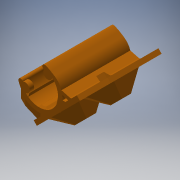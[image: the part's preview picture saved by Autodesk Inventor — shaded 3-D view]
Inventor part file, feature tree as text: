
AUTODESK INVENTOR PART (.ipt)
format: ipt  version: 2017 (Build 210142000, 142)  size: 1,034,752 bytes
history: native  units: in
note: dims shown in document units (in); Inventor stores cm internally (conversion verified against a paired STEP export)
features: other x2, extrude x2, sketch x2
ambient origin geometry x8: Origin, YZ Plane, XZ Plane, XY Plane, X Axis, Y Axis, Z Axis, Center Point
bodies: Solid1 (feature_tree)
feature tree (6):
  other  "10_Support plateau.STEP"
  extrude  "Extrusion1"  Depth=0.3937in TaperAngle=0.0deg
  extrude  "Extrusion2"  [1 undecoded]
  sketch  "Sketch1"  dims[d0=0.3937in d1=0.0in d2=0.3937in d3=0.0in]
  sketch  "Sketch2"
  parser-record x1  (decoder bookkeeping rows leaked as tree rows — omitted from the tree; the rows remain in map.json)
note: 1 required parameter value undecoded (feature->parameter linkage not recoverable at this tier; creation-order binding heuristic only, values carry confidence <= 0.55)
